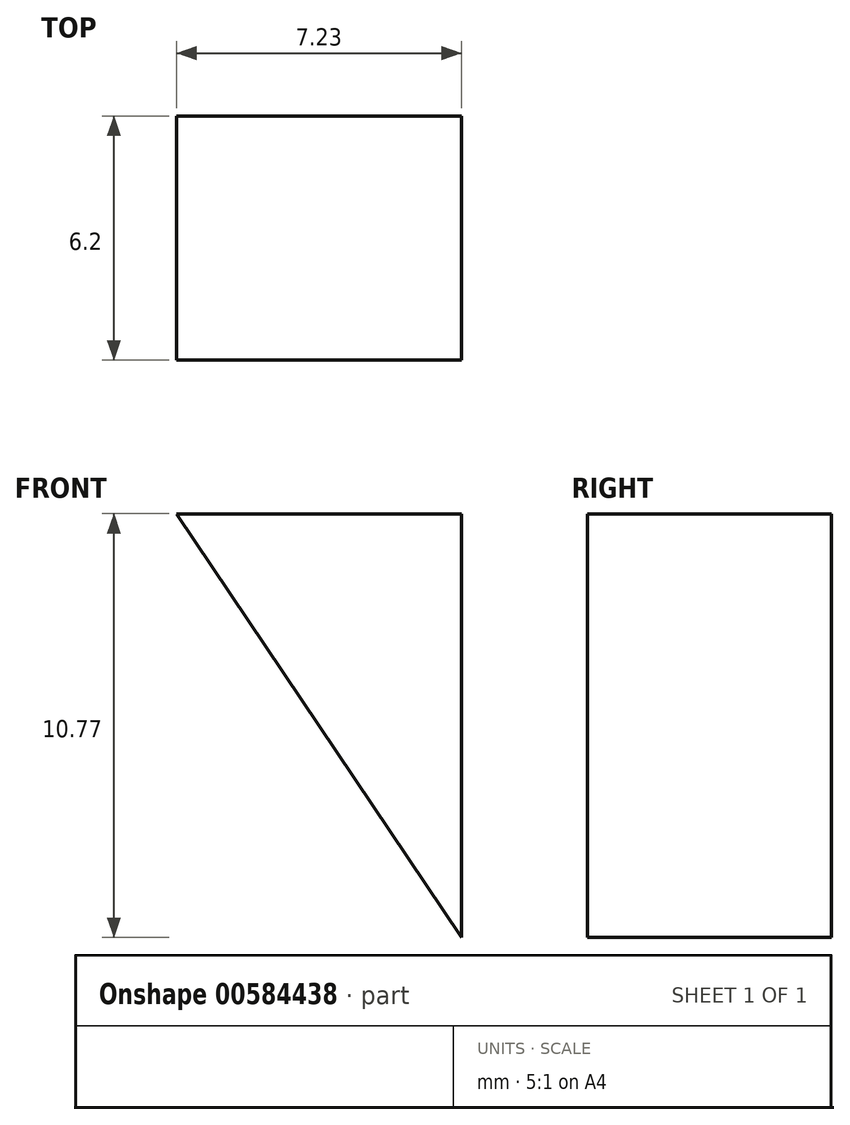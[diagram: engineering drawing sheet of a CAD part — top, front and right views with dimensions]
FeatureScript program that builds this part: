
annotation { "Feature Type Name" : "Feature", "Feature Type Description" : "" }
export const myFeature = defineFeature(function(context is Context, id is Id, definition is map)
    precondition{}
    {
        {
            var Q0;
            Q0=qCreatedBy(makeId("Front.planeOp"),FACE);
            var sketch = newSketch(context, id + "F0", { "sketchPlane" : qUnion([Q0])});
            skLineSegment(sketch, "E0", {"start": v(-35.42, 18.43) * mm, "end": v(-28.19, 18.43) * mm});
            skLineSegment(sketch, "E1", {"start": v(-28.19, 18.43) * mm, "end": v(-28.19, 7.66) * mm});
            skLineSegment(sketch, "E2", {"start": v(-28.19, 7.66) * mm, "end": v(-35.42, 18.43) * mm});
            skSolve(sketch);
        }
        {
            var Q0;
            Q0 = qSketchRegion(id + "F0", true);
            extrude(context, id + "F1", {"entities" : qUnion([Q0]), "depth" : 6.2 * mm, "offsetDistance" : 25 * mm});
        }
    });
